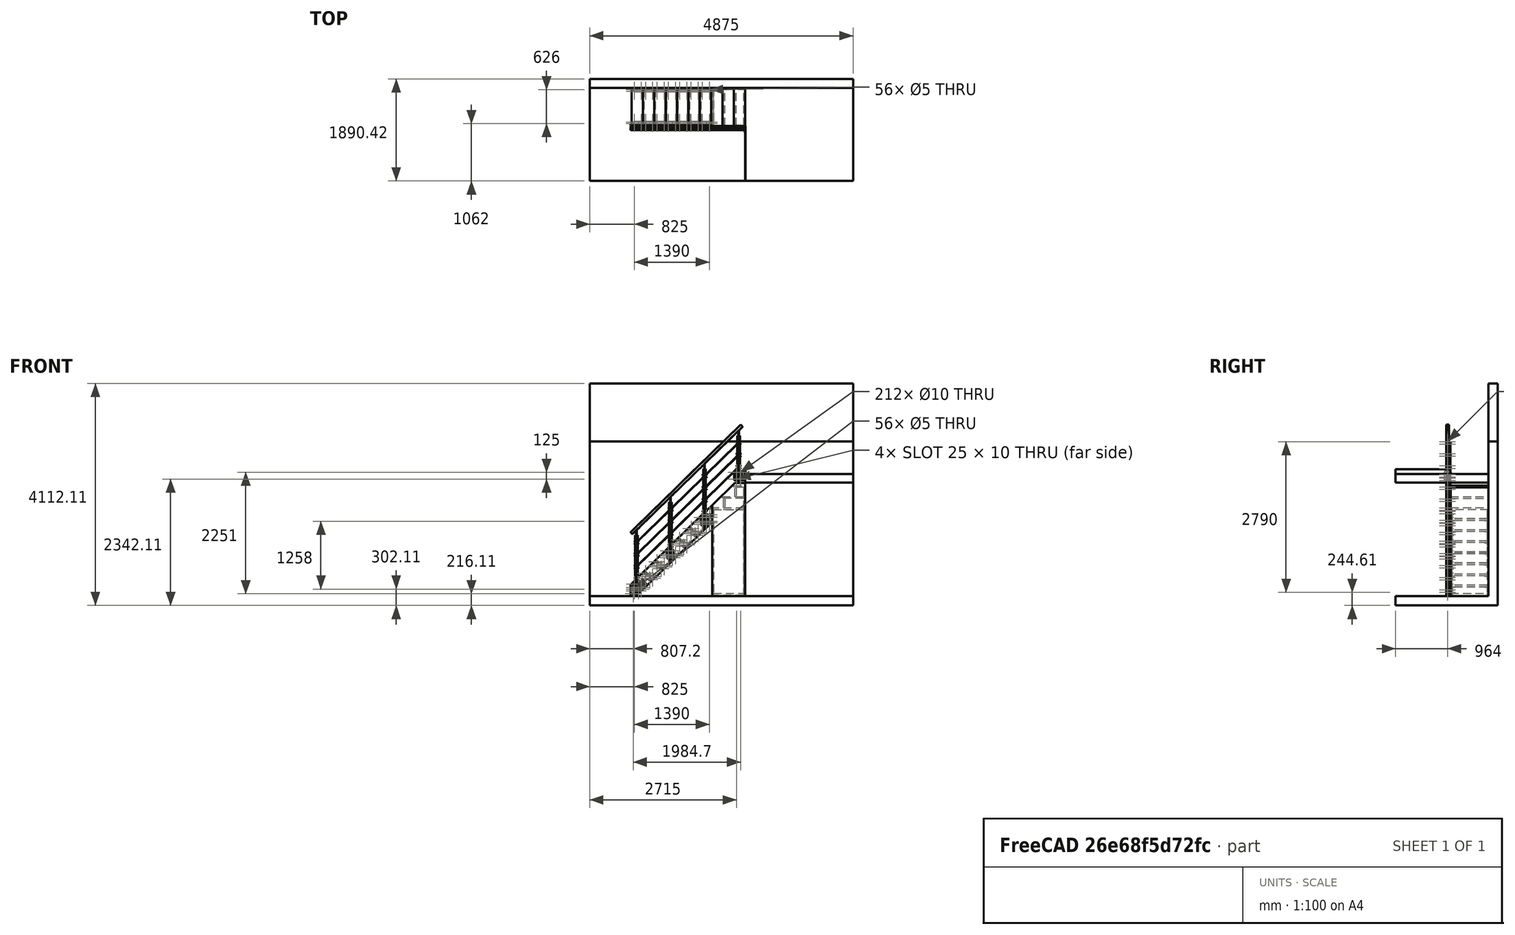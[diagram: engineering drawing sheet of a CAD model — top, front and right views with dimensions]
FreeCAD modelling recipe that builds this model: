
FCSTD DOCUMENT  (FreeCAD 0.17R11051 (Git))
Label: railing_element
License: All rights reserved
LicenseURL: http://en.wikipedia.org/wiki/All_rights_reserved
objects: Part::FeaturePython×23, Part::Compound×2, Part::Part2DObjectPython×1, Part::Extrusion×1, Part::Cut×1, App::DocumentObjectGroup×1
note: 28 computed .brp shape members not serialized (recipe doc carries the construction recipe); baked Part::Feature solids carry a one-line shape summary decoded from their .brp

FEATURE [Part::FeaturePython] double_beam_01  # a2plus imported part (geometry in sourceFile) (typed FeaturePython)
  fixedPosition = true
  sourceFile = double_beam.fcstd
  timeLastImport = 1.49424e+09
  updateColors = true
FEATURE [Part::FeaturePython] fasteners_01  # a2plus imported part (geometry in sourceFile) (typed FeaturePython)
  fixedPosition = false
  sourceFile = fasteners.fcstd
  timeLastImport = 1.49442e+09
  updateColors = true
FEATURE [Part::FeaturePython] railing_plate_01  # a2plus imported part (geometry in sourceFile) (typed FeaturePython)
  fixedPosition = false
  sourceFile = railing_plate.fcstd
  timeLastImport = 1.49443e+09
  updateColors = true
FEATURE [Part::FeaturePython] railing_dist_01  # a2plus imported part (geometry in sourceFile) (typed FeaturePython)
  fixedPosition = false
  sourceFile = railing_dist.fcstd
  timeLastImport = 1.49443e+09
  updateColors = true
FEATURE [Part::FeaturePython] railing_eyelet_01  # a2plus imported part (geometry in sourceFile) (typed FeaturePython)
  fixedPosition = false
  sourceFile = railing_eyelet.fcstd
  timeLastImport = 1.49443e+09
  updateColors = true
FEATURE [Part::FeaturePython] railing_fasteners_01  # a2plus imported part (geometry in sourceFile) (typed FeaturePython)
  fixedPosition = false
  sourceFile = railing_fasteners.fcstd
  timeLastImport = 1.49443e+09
  updateColors = true
FEATURE [Part::FeaturePython] ropes_01  # a2plus imported part (geometry in sourceFile) (typed FeaturePython)
  fixedPosition = false
  sourceFile = ropes.fcstd
  timeLastImport = 1.49443e+09
  updateColors = true
FEATURE [Part::FeaturePython] step_01  # a2plus imported part (geometry in sourceFile) (typed FeaturePython)
  fixedPosition = false
  sourceFile = step.fcstd
  timeLastImport = 1.49443e+09
  updateColors = true
FEATURE [Part::FeaturePython] handrail_holder_01  # a2plus imported part (geometry in sourceFile) (typed FeaturePython)
  fixedPosition = false
  sourceFile = handrail_holder.fcstd
  timeLastImport = 1.49443e+09
  updateColors = true
FEATURE [Part::FeaturePython] handrail_01  # a2plus imported part (geometry in sourceFile) (typed FeaturePython)
  Placement = pos=(-318.108,494.458,1490.85) rot=(0,1,0;3.93904rad)
  fixedPosition = false
  sourceFile = handrail.fcstd
  timeLastImport = 1.49444e+09
  updateColors = true
FEATURE [Part::FeaturePython] Array001  label="ropes"  # Draft array (typed FeaturePython)
  Angle = 360
  ArrayType = 0
  Axis = (0,0,1)
  Base = -> ropes_01
  Center = (0,0,0)
  Fuse = false
  IntervalAxis = (0,0,0)
  IntervalX = (630,0,615)
  IntervalY = (0,1,0)
  IntervalZ = (0,0,0)
  NumberPolar = 1
  NumberX = 3
  NumberY = 1
  NumberZ = 1
FEATURE [Part::FeaturePython] railing_wood_01  # a2plus imported part (geometry in sourceFile) (typed FeaturePython)
  fixedPosition = false
  sourceFile = railing_wood.fcstd
  timeLastImport = 1.49443e+09
  updateColors = true
FEATURE [Part::Compound] Compound
  Links = -> [railing_plate_01,handrail_holder_01,railing_fasteners_01,railing_eyelet_01,railing_dist_01,railing_wood_01]
FEATURE [Part::FeaturePython] Array  # Draft array (typed FeaturePython)
  Angle = 360
  ArrayType = 0
  Axis = (0,0,1)
  Base = -> Compound
  Center = (0,0,0)
  Fuse = false
  IntervalAxis = (0,0,0)
  IntervalX = (630,0,615)
  IntervalY = (0,1,0)
  IntervalZ = (0,0,0)
  NumberPolar = 1
  NumberX = 3
  NumberY = 1
  NumberZ = 1
FEATURE [Part::FeaturePython] fridge_box_panels_01  # a2plus imported part (geometry in sourceFile) (typed FeaturePython)
  fixedPosition = false
  sourceFile = A711_fridge_box_panels.fcstd
  timeLastImport = 1.49389e+09
  updateColors = true
FEATURE [Part::FeaturePython] fridge_box_door_01  # a2plus imported part (geometry in sourceFile) (typed FeaturePython)
  fixedPosition = false
  sourceFile = fridge_box_door.fcstd
  timeLastImport = 1.49385e+09
  updateColors = true
FEATURE [Part::FeaturePython] handrail_holder_002  # a2plus imported part (geometry in sourceFile) (typed FeaturePython)
  Placement = pos=(1890,0,1845) rot=(0,0,1;0rad)
  fixedPosition = false
  sourceFile = handrail_holder.fcstd
  timeLastImport = 1.49443e+09
  updateColors = true
FEATURE [Part::FeaturePython] railing_eyelet_002  # a2plus imported part (geometry in sourceFile) (typed FeaturePython)
  Placement = pos=(1890,0,1845) rot=(0,0,1;0rad)
  fixedPosition = false
  sourceFile = railing_eyelet.fcstd
  timeLastImport = 1.49443e+09
  updateColors = true
FEATURE [Part::FeaturePython] railing_last_wood_01  # a2plus imported part (geometry in sourceFile) (typed FeaturePython)
  Placement = pos=(1890,0,1845) rot=(0,0,1;0rad)
  fixedPosition = false
  sourceFile = railing_last_wood.fcstd
  timeLastImport = 1.49443e+09
  updateColors = true
FEATURE [Part::FeaturePython] stair_profile_01  # a2plus imported part (geometry in sourceFile) (typed FeaturePython)
  fixedPosition = false
  sourceFile = stair_profile.fcstd
  timeLastImport = 1.4938e+09
  updateColors = true
FEATURE [Part::FeaturePython] room_01  # a2plus imported part (geometry in sourceFile) (typed FeaturePython)
  fixedPosition = false
  sourceFile = room.fcstd
  timeLastImport = 1.49444e+09
  updateColors = true
FEATURE [Part::FeaturePython] plate_01  # a2plus imported part (geometry in sourceFile) (typed FeaturePython)
  fixedPosition = false
  sourceFile = plate.fcstd
  timeLastImport = 1.49399e+09
  updateColors = true
FEATURE [Part::Part2DObjectPython] Rectangle  # Draft 2D object (typed FeaturePython)
  ChamferSize = 0
  Columns = 1
  FilletRadius = 0
  Height = 1074.89
  Length = 4875
  MakeFace = true
  Placement = pos=(-775,345,2865.11) rot=(1,0,0;1.5708rad)
  Rows = 1
  Support = -> [room_01]
FEATURE [Part::Extrusion] Extrude
  Base = -> Rectangle
  Dir = (0,1,0)
  DirMode = 0
  FaceMakerClass = Part::FaceMakerBullseye
  LengthFwd = 500
  LengthRev = 0
  Solid = false
  Symmetric = false
FEATURE [Part::Cut] Cut  label="Cutted_room"
  Base = -> room_01
  Tool = -> Extrude
FEATURE [Part::FeaturePython] room_002  # a2plus imported part (geometry in sourceFile) (typed FeaturePython)
  fixedPosition = false
  sourceFile = room.fcstd
  timeLastImport = 1.49444e+09
  updateColors = true
FEATURE [App::DocumentObjectGroup] Group  label="ref"
  Group = -> [double_beam_01,fasteners_01,step_01,Array001,fridge_box_panels_01,fridge_box_door_01,stair_profile_01,plate_01,Cut,room_002]
FEATURE [Part::FeaturePython] railing_last_steel_02  # a2plus imported part (geometry in sourceFile) (typed FeaturePython)
  Placement = pos=(1890,0,2070) rot=(0,0,1;0rad)
  fixedPosition = false
  sourceFile = railing_last_steel.fcstd
  timeLastImport = 1.49451e+09
  updateColors = true
FEATURE [Part::Compound] Compound001  label="last_railing"
  Links = -> [handrail_holder_002,railing_eyelet_002,railing_last_wood_01,railing_last_steel_02]
